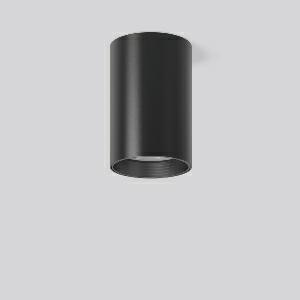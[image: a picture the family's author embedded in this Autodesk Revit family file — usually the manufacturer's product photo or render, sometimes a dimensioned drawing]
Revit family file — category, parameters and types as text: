
# Revit family: heledon_maxi_a_931242_003_15d9
name_source: partatom
category: Lighting Fixtures
units: mm (PartAtom-declared; Revit-internal decimal feet)

## family parameters
Cut with Voids When Loaded = No
Host = Face
Light Source = No
Part Type = Normal
Room Calculation Point = No
Round Connector Dimension = Use Diameter
Shared = No

## types (1)
- HELEDON maxi A (1 x LED Modul 920 meat+, 1850 lm, 2000)
    Apparent Load = 33 VA
    Approval mark = CE
    CIE Flux Codes = 96 99 100 100 100
    Color Rendering = 90
    Color Temperature = 2000
    Default Elevation = 1800 mm
    Description = Series: HELEDON maxi
Cylindrical surface-mounted downlight. Housing: die-cast aluminium, powder-coated. Internal ceiling frame polycarbonate with bayonet mounting. Black plastic ring and recessed LED to prevent glare from the side. Optical assembly with lens made of plastic (polycarbonate) for the best homogeneous light distribution - can be changed without tools. Special LED for illumination of meat included. Suitable for Ceiling mounting. Easy installation with a separate ceiling frame with bayonet mounting and plug connection. Driver integrated. Connected via plug-in connector. High quality converter without flickering and stroboscopic effect. The following accessories can be mounted without use of tools: interchangeable lenses, decorative glasses, honeycomb louvre, clear and frosted diffusers, white interchangeable plastic ring. 
Colour: deep black, matt (RAL 9005)
Diameter: 123 mm
Height: 183 mm
Lamp: LED
Socket: without socket
Colour temperature: meat +
System power: 33 W
Rated luminous flux: 1850 lm
Luminous efficiency: 56 lm/W
Control gear: Regulated power supply
Protection class: I
Type of protection: IP 20
    Height = 183 mm
    Lamp = 1 x LED Modul 920 meat+
    Lamp Light Flux = 1850 lm
    Lamp count = 1
    Length = 123 mm
    Lifetime = 50000 h
    Luminous efficacy = 56 lm/W
    Manufacturer = RZB
    ModVariant = No
    Model = 931242.003
    Mounting Place = Ceiling
    Mounting Type = Surface mounted
    Number of Poles = 1
    OnlyDefault = Yes
    Power Factor = 1
    Product Name = HELEDON maxi A
    Product group = Surface mounted downlights
    ProductGroupID = 302
    Protection Class = Protection class I
    Protection Degree = IP 20
    RLX_Detail_Level = 1
    RLX_Emergency_Light_Flux = 0 lm
    RLX_Emergency_Type = 0
    RLX_Emergency_Type_DB = No
    RlxData = <blob elided: 97573 chars, md5=8e03b14b>
    Socket = socket
    Standby Power = 0 W
    System Light Flux = 1850 lm
    System Power = 33 W
    Type Comments = Product without accessories
    Type Image = 931193.003.jpg
    URL = http://relux.com
    VarID = ---
    Voltage = 230 V
    Voltage Range = 220-240 V
    Weight = 0.00 kg
    Width = 0 mm  [stored 0 ft]

note: [stored X ft] marks values corroborated as IEEE doubles in the binary element streams (Revit-internal decimal feet)

## geometry (parser evidence)
native form markers: Blend x4, Sweep x9
no freeform markers — native parametric forms only
